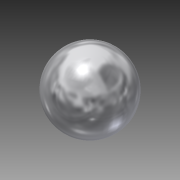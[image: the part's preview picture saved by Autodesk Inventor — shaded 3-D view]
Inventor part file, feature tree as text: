
AUTODESK INVENTOR PART (.ipt)
format: ipt  version: 2014 (Build 180170000, 170)  size: 114,176 bytes
history: native  units: in
note: dims shown in document units (in); Inventor stores cm internally (conversion verified against a paired STEP export)
features: extrude x2, fillet x2, sketch x2
ambient origin geometry x8: Origin, YZ Plane, XZ Plane, XY Plane, X Axis, Y Axis, Z Axis, Center Point
bodies: Solid1 (feature_tree)
feature tree (6):
  extrude  "Extrusion1"  Depth=0.25in TaperAngle=0.0deg
  fillet  "Fillet1"  Radius=0.25in
  extrude  "Extrusion2"  Depth=0.25in TaperAngle=0.0deg
  fillet  "Fillet2"  Radius=0.25in
  sketch  "Sketch1"  dims[d0=0.5in d1=0.25in d2=0.0in d3=0.25in]
  sketch  "Sketch2"  dims[d4=0.5in d5=0.25in d6=0.0in d7=0.25in]
